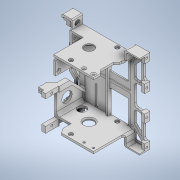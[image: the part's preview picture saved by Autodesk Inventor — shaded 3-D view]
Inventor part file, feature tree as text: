
AUTODESK INVENTOR PART (.ipt)
format: ipt  version: 2021 (Build 250183000, 183)  size: 1,649,152 bytes
history: native  units: mm
features: sketch x89, extrude x75, chamfer x22, fillet x15, hole x14
ambient origin geometry x8: Origin, YZ Plane, XZ Plane, XY Plane, X Axis, Y Axis, Z Axis, Center Point
bodies: Solid1 (feature_tree)
feature tree (215):
  extrude  "Extrusion1"  Depth=60.0mm
  extrude  "Extrusion3"  Depth=2.0mm
  extrude  "Extrusion4"  Depth=40.0mm TaperAngle=0.0deg
  hole  "Hole1"  [1 undecoded]
  hole  "Hole2"  [1 undecoded]
  extrude  "Extrusion5"  Depth=4.0mm
  extrude  "Extrusion6"  Depth=33.0mm
  extrude  "Extrusion7"  Depth=2.0mm
  extrude  "Extrusion8"  Depth=0.8mm TaperAngle=0.0deg
  extrude  "Extrusion9"  Depth=4.0mm
  extrude  "Extrusion10"  Depth=4.0mm
  extrude  "Extrusion11"  Depth=1.0mm
  chamfer  "Chamfer1"  Distance=2.0mm
  fillet  "Fillet1"  Radius=0.4mm
  hole  "Hole3"  [1 undecoded]
  chamfer  "Chamfer2"  Distance=12.4mm
  extrude  "Extrusion12"  Depth=2.0mm TaperAngle=0.0deg
  extrude  "Extrusion13"  Depth=2.0mm TaperAngle=0.0deg
  extrude  "Extrusion14"  Depth=4.4mm
  hole  "Hole4"  [1 undecoded]
  extrude  "Extrusion15"  Depth=2.4mm
  extrude  "Extrusion16"  Depth=1.0mm TaperAngle=45.0deg
  chamfer  "Chamfer3"  Distance=37.6mm
  extrude  "Extrusion17"  Depth=2.0mm TaperAngle=0.0deg
  extrude  "Extrusion18"  Depth=2.4mm
  extrude  "Extrusion19"  Depth=16.0mm
  extrude  "Extrusion20"  Depth=15.0mm
  extrude  "Extrusion21"  Depth=20.0mm TaperAngle=0.0deg
  extrude  "Extrusion22"  Depth=0.8mm TaperAngle=0.0deg
  extrude  "Extrusion23"  Depth=30.0mm
  hole  "Hole5"  [1 undecoded]
  extrude  "Extrusion24"  Depth=20.0mm TaperAngle=0.0deg
  extrude  "Extrusion26"  Depth=2.0mm TaperAngle=0.0deg
  extrude  "Extrusion27"  Depth=9.0mm
  extrude  "Extrusion28"  Depth=3.0mm TaperAngle=0.0deg
  extrude  "Extrusion29"  Depth=6.0mm
  extrude  "Extrusion30"  Depth=2.0mm
  hole  "Hole6"  [1 undecoded]
  chamfer  "Chamfer4"  Distance=17.0mm
  chamfer  "Chamfer5"  Distance=2.0mm
  extrude  "Extrusion32"  Depth=28.0mm
  chamfer  "Chamfer6"  Distance=2.0mm
  extrude  "Extrusion33"  Depth=6.0mm
  fillet  "Fillet2"  Radius=5.0mm
  extrude  "Extrusion34"  TaperAngle=0.0deg  [1 undecoded]
  extrude  "Extrusion35"  Depth=5.0mm TaperAngle=45.0deg
  extrude  "Extrusion36"  Depth=5.0mm
  extrude  "Extrusion37"  Depth=8.0mm TaperAngle=45.0deg
  extrude  "Extrusion38"  Depth=3.0mm
  fillet  "Fillet3"  Radius=10.0mm
  extrude  "Extrusion39"  Depth=10.0mm
  fillet  "Fillet4"  Radius=2.0mm
  extrude  "Extrusion40"  Depth=0.5mm
  extrude  "Extrusion41"  Depth=0.5mm TaperAngle=0.0deg
  extrude  "Extrusion42"  Depth=2.0mm
  extrude  "Extrusion43"  Depth=10.0mm
  hole  "Hole7"  [1 undecoded]
  hole  "Hole8"  [1 undecoded]
  hole  "Hole9"  [1 undecoded]
  hole  "Hole10"  [1 undecoded]
  extrude  "Extrusion44"  Depth=2.0mm TaperAngle=0.0deg
  chamfer  "Chamfer7"  Distance=2.0mm
  extrude  "Extrusion45"  Depth=5.0mm TaperAngle=0.0deg
  extrude  "Extrusion46"  Depth=10.0mm
  extrude  "Extrusion47"  Depth=3.0mm
  extrude  "Extrusion48"  Depth=2.2mm
  extrude  "Extrusion50"  Depth=3.0mm
  fillet  "Fillet7"  Radius=3.0mm
  extrude  "Extrusion52"  Depth=3.0mm
  chamfer  "Chamfer9"  Distance=2.0mm
  chamfer  "Chamfer10"  Distance=1.2mm Angle=45.0deg
  chamfer  "Chamfer11"  Distance=2.0mm
  extrude  "Extrusion54"  Depth=10.0mm
  extrude  "Extrusion55"  Depth=8.5mm
  extrude  "Extrusion56"  Depth=2.0mm
  extrude  "Extrusion57"  Depth=64.0mm
  chamfer  "Chamfer12"  Distance=2.0mm
  extrude  "Extrusion58"  Depth=2.0mm TaperAngle=0.0deg
  extrude  "Extrusion59"  Depth=5.0mm
  fillet  "Fillet9"  Radius=40.5mm
  hole  "Hole11"  [1 undecoded]
  fillet  "Fillet10"  Radius=76.03mm
  chamfer  "Chamfer13"  Distance=2.0mm
  extrude  "Extrusion60"  Depth=2.0mm
  extrude  "Extrusion61"  Depth=2.0mm
  extrude  "Extrusion62"  Depth=2.0mm
  extrude  "Extrusion63"  Depth=2.0mm
  extrude  "Extrusion64"  Depth=2.0mm
  extrude  "Extrusion65"  Depth=2.0mm
  chamfer  "Chamfer14"  Distance=2.0mm
  chamfer  "Chamfer15"  Distance=2.0mm
  extrude  "Extrusion66"  Depth=2.0mm
  extrude  "Extrusion67"  Depth=7.0mm TaperAngle=0.0deg
  fillet  "Fillet12"  Radius=2.0mm
  extrude  "Extrusion68"  Depth=1.0mm
  chamfer  "Chamfer16"  Distance=2.0mm
  fillet  "Fillet14"  Radius=4.0mm
  extrude  "Extrusion69"  Depth=2.0mm TaperAngle=45.0deg
  fillet  "Fillet15"  Radius=1.0mm
  extrude  "Extrusion70"  Depth=2.0mm TaperAngle=0.0deg
  extrude  "Extrusion71"  Depth=2.0mm
  chamfer  "Chamfer17"  Distance=8.0mm
  hole  "Hole12"  [1 undecoded]
  extrude  "Extrusion72"  Depth=2.0mm TaperAngle=0.0deg
  extrude  "Extrusion73"  Depth=5.0mm
  hole  "Hole13"  [1 undecoded]
  extrude  "Extrusion74"  Depth=1.2mm TaperAngle=45.0deg
  extrude  "Extrusion75"  Depth=2.0mm TaperAngle=0.0deg
  extrude  "Extrusion76"  Depth=1.0mm TaperAngle=0.0deg
  chamfer  "Chamfer18"  Distance=1.0mm
  chamfer  "Chamfer19"  Distance=2.5mm
  chamfer  "Chamfer20"  Distance=2.5mm
  extrude  "Extrusion77"  Depth=4.0mm
  fillet  "Fillet16"  Radius=13.0mm
  fillet  "Fillet17"  Radius=2.0mm
  extrude  "Extrusion78"  Depth=2.5mm
  fillet  "Fillet18"  Radius=1.0mm
  extrude  "Extrusion79"  Depth=1.2mm TaperAngle=45.0deg
  chamfer  "Chamfer21"  Distance=2.0mm
  extrude  "Extrusion80"  Depth=2.0mm
  chamfer  "Chamfer22"  Distance=14.0mm
  hole  "Hole14"  [1 undecoded]
  extrude  "Extrusion81"  Depth=0.6mm
  chamfer  "Chamfer23"  Distance=12.4mm
  fillet  "Fillet19"  Radius=15.0mm
  fillet  "Fillet20"  Radius=2.0mm
  sketch  "Sketch1"  dims[d0=48.0mm d1=60.0mm]
  sketch  "Sketch3"  dims[d2=1.2mm d3=0.0mm d6=2.0mm]
  sketch  "Sketch4"  dims[d7=2.0mm d8=40.0mm d9=0.0mm]
  sketch  "Sketch5"  dims[d10=16.8mm d11=21.0mm]
  sketch  "Sketch6"  dims[d12=9.2mm d13=80.0mm d14=0.0mm]
  sketch  "Sketch7"  dims[d15=4.0mm d16=22.7mm]
  sketch  "Sketch8"  dims[d17=11.8mm d18=33.0mm]
  sketch  "Sketch9"  dims[d19=4.0mm d20=6.0mm d21=6.0mm d22=2.0mm d23=90.0deg d24=4.0mm d25=20.594885mm]
  sketch  "Sketch10"  dims[d26=4.0mm d27=6.0mm d28=6.0mm d29=2.0mm d30=90.0deg d31=4.0mm d32=20.594885mm d33=2.0mm]
  sketch  "Sketch11"  dims[d34=2.0mm d35=0.8mm d36=0.0mm]
  sketch  "Sketch12"  dims[d37=4.0mm d38=4.0mm]
  sketch  "Sketch13"  dims[d39=1.0mm d40=4.0mm]
  sketch  "Sketch14"  dims[d41=4.0mm d42=1.0mm]
  sketch  "Sketch15"  dims[d43=3.0mm d44=2.0mm d45=0.0mm d46=0.4mm d47=0.0mm]
  sketch  "Sketch16"  dims[d48=12.0mm d49=22.0mm]
  sketch  "Sketch17"  dims[d50=12.4mm d51=12.4mm d52=0.0mm]
  sketch  "Sketch18"  dims[d53=8.0mm d54=2.0mm d55=0.0mm]
  sketch  "Sketch19"  dims[d56=8.0mm d57=2.0mm d58=0.0mm]
  sketch  "Sketch20"  dims[d59=0.4mm d60=4.4mm]
  sketch  "Sketch21"  dims[d61=12.4mm d62=0.0mm d63=2.4mm d64=2.0mm d65=45.0deg]
  sketch  "Sketch22"  dims[d66=2.0mm d67=2.4mm]
  sketch  "Sketch23"  dims[d68=6.0mm]
  sketch  "Sketch24"  dims[d69=2.0mm d70=6.0mm d71=3.0mm d72=2.0mm d73=90.0deg d74=5.0mm d75=20.594885mm d76=1.0mm d77=2.0mm d78=45.0deg]
  sketch  "Sketch25"  dims[d79=22.0mm]
  sketch  "Sketch26"  dims[d80=5.0mm]
  sketch  "Sketch27"  dims[d81=4.4mm]
  sketch  "Sketch28"  dims[d82=4.4mm d83=37.6mm d84=0.0mm]
  sketch  "Sketch29"  dims[d85=4.4mm d86=0.0mm d87=2.0mm d88=0.0mm]
  sketch  "Sketch31"  dims[d89=6.0mm d90=2.4mm]
  sketch  "Sketch32"  dims[d91=27.2mm]
  sketch  "Sketch33"  dims[d92=2.0mm d93=6.0mm d94=3.0mm d95=2.0mm d96=90.0deg d97=5.0mm d98=20.594885mm d99=16.0mm]
  sketch  "Sketch34"  dims[d100=2.0mm d101=0.0mm d102=15.0mm]
  sketch  "Sketch35"  dims[d103=8.0mm d104=20.0mm d105=0.0mm]
  sketch  "Sketch36"  dims[d106=2.0mm d107=2.0mm d108=45.0deg d109=0.8mm d110=0.0mm]
  sketch  "Sketch38"  dims[d111=60.0mm d112=30.0mm]
  sketch  "Sketch39"  dims[d113=1.0mm d114=1.0mm]
  sketch  "Sketch40"  dims[d115=0.8mm d116=0.0mm d117=20.0mm d118=0.0mm]
  sketch  "Sketch41"  dims[d119=20.0mm d120=0.0mm d121=2.0mm d122=0.0mm]
  sketch  "Sketch42"  dims[d123=17.0mm d124=9.0mm]
  sketch  "Sketch43"  dims[d125=10.0mm d126=0.0mm d127=3.0mm d128=0.0mm]
  sketch  "Sketch44"  dims[d129=6.0mm d130=9.6mm]
  sketch  "Sketch45"  dims[d131=2.0mm d132=6.0mm d133=3.0mm d134=2.0mm d135=90.0deg d136=5.0mm d137=20.594885mm d138=2.0mm]
  sketch  "Sketch46"  dims[d139=2.0mm d140=10.0mm d141=0.0mm]
  sketch  "Sketch47"  dims[d145=0.2mm d146=17.0mm d147=0.0mm d148=2.0mm d149=0.0mm]
  sketch  "Sketch48"  dims[d150=11.7mm d151=28.0mm d152=2.0mm d153=0.0mm]
  sketch  "Sketch49"  dims[d154=2.0mm d155=6.0mm d156=5.0mm d157=0.0mm]
  sketch  "Sketch50"  dims[d158=33.4mm d159=0.0mm d160=0.0mm]
  sketch  "Sketch51"  dims[d161=27.2mm]
  sketch  "Sketch52"  dims[d162=2.0mm d163=6.0mm d164=3.0mm d165=2.0mm d166=90.0deg d167=5.0mm d168=20.594885mm d169=5.0mm d170=2.0mm d171=45.0deg]
  sketch  "Sketch53"  dims[d172=5.6mm d173=2.0mm d174=45.0deg d181=5.0mm]
  sketch  "Sketch54"  dims[d182=2.0mm d183=0.0mm d184=8.0mm d185=2.0mm d186=45.0deg]
  sketch  "Sketch55"  dims[d187=20.0mm d188=0.0mm d189=3.0mm d190=10.0mm]
  sketch  "Sketch56"  dims[d191=10.0mm d192=10.0mm d193=2.0mm d194=0.0mm]
  sketch  "Sketch57"  dims[d195=23.0mm d196=0.5mm]
  sketch  "Sketch58"  dims[d197=0.5mm d198=12.4mm d199=0.0mm]
  sketch  "Sketch60"  dims[d200=10.0mm d201=0.0mm d202=2.0mm]
  sketch  "Sketch62"  dims[d203=2.4mm d204=0.0mm d205=10.0mm]
  sketch  "Sketch64"  dims[d206=5.0mm d207=5.0mm d208=0.0mm]
  sketch  "Sketch65"  dims[d209=1.0mm d210=4.0mm]
  sketch  "Sketch66"  dims[d211=4.0mm d212=20.0mm]
  sketch  "Sketch67"  dims[d213=4.0mm d214=4.0mm]
  sketch  "Sketch68"  dims[d215=20.0mm d216=2.0mm d217=0.0mm]
  sketch  "Sketch69"  dims[d218=1.0mm]
  sketch  "Sketch70"  dims[d219=2.0mm d220=2.0mm d221=0.0mm]
  sketch  "Sketch71"  dims[d222=2.0mm d223=0.0mm d224=5.0mm d225=0.0mm]
  sketch  "Sketch72"  dims[d226=5.0mm d227=0.0mm d228=10.0mm]
  sketch  "Sketch73"  dims[d229=10.0mm d230=3.0mm]
  sketch  "Sketch74"  dims[d231=9.0mm d232=2.2mm]
  sketch  "Sketch75"  dims[d233=2.0mm d234=6.0mm d235=4.0mm d236=2.0mm d237=90.0deg d238=3.0mm d239=20.594885mm d240=3.0mm d241=3.0mm]
  sketch  "Sketch76"  dims[d242=2.0mm d243=6.0mm d244=4.0mm d245=2.0mm d246=90.0deg d247=3.0mm d248=20.594885mm d249=3.0mm]
  sketch  "Sketch77"  dims[d250=3.0mm]
  sketch  "Sketch78"  dims[d251=3.0mm]
  sketch  "Sketch79"  dims[d252=12.0mm]
  sketch  "Sketch80"  dims[d253=2.0mm d254=6.0mm d255=4.0mm d256=2.0mm d257=90.0deg d258=3.0mm d259=20.594885mm]
  sketch  "Sketch81"  dims[d260=2.0mm d261=6.0mm d262=4.0mm d263=2.0mm d264=90.0deg d265=3.0mm d266=20.594885mm]
  sketch  "Sketch82"  dims[d267=5.2mm]
  sketch  "Sketch83"  dims[d268=1.2mm]
  sketch  "Sketch84"  dims[d269=1.0mm]
  sketch  "Sketch85"  dims[d270=1.0mm d271=2.0mm d272=0.0mm d273=1.2mm d274=2.0mm d275=45.0deg d276=2.0mm d277=0.0mm]
  sketch  "Sketch86"  dims[d278=81.0mm d279=10.0mm]
  sketch  "Sketch87"  dims[d280=70.0mm d281=8.5mm]
  sketch  "Sketch88"  dims[d282=2.0mm d283=2.0mm]
  sketch  "Sketch89"  dims[d284=2.0mm d285=64.0mm]
  sketch  "Sketch90"  dims[d286=8.5mm d287=2.0mm d288=0.0mm]
  sketch  "Sketch91"  dims[d289=21.4mm d290=2.0mm d291=0.0mm]
  sketch  "Sketch92"  dims[d295=5.0mm d296=5.0mm d297=40.5mm]
  sketch  "Sketch93"  dims[d298=5.0mm d299=5.0mm d300=76.03mm]
  sketch  "Sketch94"  dims[d301=2.0mm]
  sketch  "Sketch95"  dims[d302=2.0mm d303=2.0mm d304=2.0mm d305=2.0mm d306=2.0mm d307=2.0mm d308=2.0mm d309=2.0mm d310=2.0mm d311=2.0mm d312=2.0mm d313=7.0mm d314=0.0mm d322=2.0mm d323=0.0mm d331=1.0mm d332=2.0mm d333=0.0mm d334=4.0mm d335=2.0mm d336=45.0deg d337=2.0mm d338=2.0mm d339=45.0deg d343=1.0mm d344=2.0mm d345=45.0deg d346=2.0mm d347=0.0mm d348=2.0mm d349=8.0mm d350=0.0mm d351=5.0mm d352=2.0mm d353=0.0mm d354=5.0mm d355=4.0mm d356=0.0mm d357=1.2mm d358=2.0mm d359=45.0deg d360=2.0mm d361=0.0mm d362=1.0mm d363=0.0mm d364=1.0mm d365=2.5mm d366=2.5mm d367=4.0mm d368=13.0mm d369=2.0mm d370=2.5mm d371=2.0mm d372=6.0mm d373=4.0mm d374=2.0mm d375=90.0deg d376=3.0mm d377=20.594885mm d378=1.0mm d379=1.2mm d380=2.0mm d381=45.0deg d382=2.0mm d383=2.0mm d384=14.0mm d385=2.0mm d386=0.0mm d387=0.6mm d388=12.4mm d389=0.0mm d390=15.0mm d391=2.0mm d392=2.0mm d393=2.0mm d394=2.0mm d395=2.0mm d396=0.0mm d397=3.0mm d398=3.0mm d399=28.0mm d400=3.0mm d401=3.0mm d402=53.0mm d403=3.0mm d404=78.0mm d405=2.0mm d406=2.0mm d407=2.0mm d408=2.0mm d409=2.0mm d410=2.0mm d411=2.0mm d412=2.0mm d413=2.0mm d414=2.0mm d415=2.0mm d416=2.0mm d417=2.0mm d418=2.0mm d419=2.0mm d420=2.0mm d421=4.0mm d422=0.0mm d423=2.0mm d424=0.0mm d425=45.0deg d426=2.0mm d427=2.0mm d428=2.0mm d429=0.0mm d430=2.0mm d431=2.0mm d432=45.0deg d434=1.0mm d435=2.0mm d436=45.0deg d437=2.0mm d438=0.0mm d439=2.0mm d440=2.0mm d441=0.0mm d442=1.0mm d443=1.2mm d444=1.2mm d445=8.0mm d446=0.0mm d448=2.0mm d449=2.0mm d450=45.0deg d451=2.0mm d452=2.0mm d453=0.0mm d454=3.0mm d455=1.6mm d456=1.6mm d457=4.0mm d458=8.0mm d459=2.0mm d460=0.0mm d461=3.0mm d462=10.0mm d463=15.0mm d464=2.0mm d465=0.0mm d466=3.0mm d467=2.0mm d468=45.0deg d469=2.5mm d470=2.0mm d471=5.0mm d472=5.0mm d473=2.0mm d474=2.0mm d475=6.0mm d476=4.0mm d477=2.0mm d478=90.0deg d479=3.0mm d480=20.594885mm d481=2.0mm d482=6.0mm d483=7.0mm d484=0.0mm d485=45.0deg d486=4.5mm d487=0.0mm d488=3.0mm d489=2.7mm d490=2.0mm d491=6.0mm d492=4.0mm d493=2.0mm d494=90.0deg d495=3.0mm d496=20.594885mm d497=2.0mm d498=8.0mm d499=0.0mm d500=2.0mm d501=0.0mm d502=2.0mm d503=2.0mm d504=2.0mm d505=2.0mm d506=2.0mm d507=0.0mm d508=3.0mm d509=2.0mm d510=45.0deg d511=2.0mm d512=2.0mm d513=45.0deg d514=2.0mm d515=2.0mm d516=45.0deg d517=2.0mm d518=2.0mm d519=2.0mm d520=0.0mm d521=2.0mm d522=2.0mm d523=2.0mm d524=2.0mm d525=20.0mm d526=20.0mm d527=2.0mm d528=0.0mm d529=1.0mm d530=3.0mm d531=2.5mm d532=3.0mm d533=2.5mm d534=7.0mm d535=0.0mm d536=1.0mm d537=2.0mm d538=45.0deg d539=7.0mm d540=0.0mm d541=1.0mm d542=2.0mm d543=45.0deg d544=2.1mm d545=6.0mm d546=4.0mm d547=2.0mm d548=90.0deg d549=10.0mm d550=20.594885mm d551=2.0mm d552=2.0mm d553=2.0mm d554=2.0mm d555=2.0mm d556=2.0mm d557=4.0mm d558=0.0mm d559=1.0mm d560=2.0mm d561=45.0deg d562=2.0mm d563=2.0mm d324=0.5mm d325=0.872665mm d326=0.5mm d327=0.872665mm]
note: 15 required parameter values undecoded (feature->parameter linkage not recoverable at this tier; creation-order binding heuristic only, values carry confidence <= 0.55)
